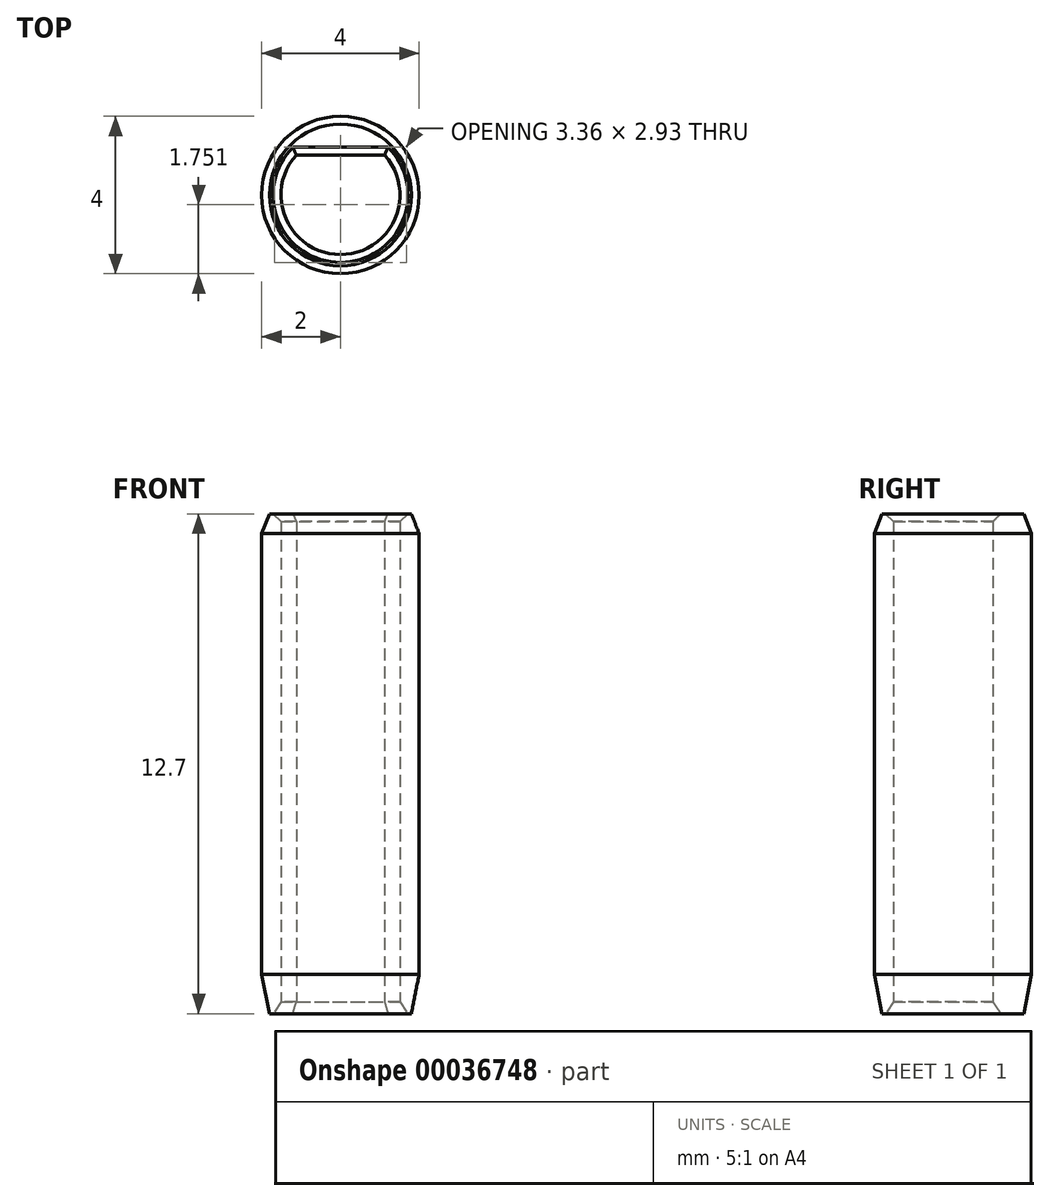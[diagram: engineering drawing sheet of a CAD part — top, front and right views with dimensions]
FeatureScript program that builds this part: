
annotation { "Feature Type Name" : "Feature", "Feature Type Description" : "" }
export const myFeature = defineFeature(function(context is Context, id is Id, definition is map)
    precondition{}
    {
        {
            var Q0;
            Q0=qCreatedBy(makeId("Top.planeOp"),FACE);
            var sketch = newSketch(context, id + "F0", { "sketchPlane" : qUnion([Q0])});
            skCircle(sketch, "E0", {"center": v(0, 0) * mm, "radius": 2 * mm});
            skCircle(sketch, "E1", {"center": v(0, 0) * mm, "radius": 1.51 * mm});
            skLineSegment(sketch, "E2", {"start": v(0, 1.51) * mm, "end": v(-2.54, 1.51) * mm, "construction": true});
            skLineSegment(sketch, "E3", {"start": v(-2.54, 1.51) * mm, "end": v(2.5, 1.51) * mm, "construction": true});
            skLineSegment(sketch, "E4", {"start": v(-1.51, 0) * mm, "end": v(-1.51, 1.51) * mm, "construction": true});
            skLineSegment(sketch, "E5", {"start": v(1.51, 0) * mm, "end": v(1.51, 1.51) * mm, "construction": true});
            skPoint(sketch, "E6", {"position": v(0, 1.01) * mm});
            skLineSegment(sketch, "E7", {"start": v(0, 1.01) * mm, "end": v(-1.12, 1.01) * mm});
            skLineSegment(sketch, "E8", {"start": v(0, 1.01) * mm, "end": v(1.12, 1.01) * mm});
            skSolve(sketch);
        }
        {
            var Q0;
            Q0=makeQuery(id+"F0.imprint","IMPRINT",FACE,{"disambiguationData":[TD([[makeQuery(id+"F0.imprint","IMPRINT",EDGE,{"derivedFrom":sQuery(id+"F0.wireOp",EDGE,"E0")}),1.0]])]});
            var Q1;
            {var subQ1=sQuery(id+"F0.wireOp",EDGE,"E7");Q1=makeQuery(id+"F0.imprint","IMPRINT",FACE,{"disambiguationData":[TD([[makeQuery(id+"F0.imprint","IMPRINT",EDGE,{"derivedFrom":subQ1}),-1.0]])]});}
            extrude(context, id + "F1", {"entities" : qUnion([Q0, Q1]), "depth" : 12.7 * mm});
        }
        {
            var Q0;
            Q0=makeQuery(id+"F1.opExtrude","CAP_EDGE",EDGE,{"disambiguationData":[OSD([sQuery(id+"F0.wireOp",EDGE,"E0")])],"isStart":true});
            chamfer(context, id + "F2", {"entities" : qUnion([Q0]), "chamferType" : ChamferType.TWO_OFFSETS, "width1" : 1 * mm, "oppositeDirection" : false, "width2" : 0.2 * mm, "tangentPropagation" : true});
        }
        {
            var Q0;
            Q0=makeQuery(id+"F1.opExtrude","CAP_EDGE",EDGE,{"disambiguationData":[OSD([sQuery(id+"F0.wireOp",EDGE,"E0")])],"isStart":false});
            chamfer(context, id + "F3", {"entities" : qUnion([Q0]), "chamferType" : ChamferType.TWO_OFFSETS, "width1" : 0.2 * mm, "oppositeDirection" : false, "width2" : 0.5 * mm, "tangentPropagation" : true});
        }
        {
            var Q0;
            Q0=makeQuery(id+"F1.opExtrude","CAP_EDGE",EDGE,{"disambiguationData":[OSD([sQuery(id+"F0.wireOp",EDGE,"E7"),sQuery(id+"F0.wireOp",EDGE,"E8")])],"isStart":false});
            var Q1;
            Q1=makeQuery(id+"F1.opExtrude","CAP_EDGE",EDGE,{"disambiguationData":[OSD([sQuery(id+"F0.wireOp",EDGE,"E1")])],"isStart":false});
            chamfer(context, id + "F4", {"entities" : qUnion([Q0, Q1]), "width" : 0.2 * mm, "tangentPropagation" : true});
        }
        {
            var Q0;
            Q0=makeQuery(id+"F1.opExtrude","CAP_EDGE",EDGE,{"disambiguationData":[OSD([sQuery(id+"F0.wireOp",EDGE,"E1")])],"isStart":true});
            var Q1;
            Q1=makeQuery(id+"F1.opExtrude","CAP_EDGE",EDGE,{"disambiguationData":[OSD([sQuery(id+"F0.wireOp",EDGE,"E7"),sQuery(id+"F0.wireOp",EDGE,"E8")])],"isStart":true});
            chamfer(context, id + "F5", {"entities" : qUnion([Q0, Q1]), "chamferType" : ChamferType.TWO_OFFSETS, "width1" : 0.2 * mm, "oppositeDirection" : false, "width2" : 0.3 * mm, "tangentPropagation" : true});
        }
    });
